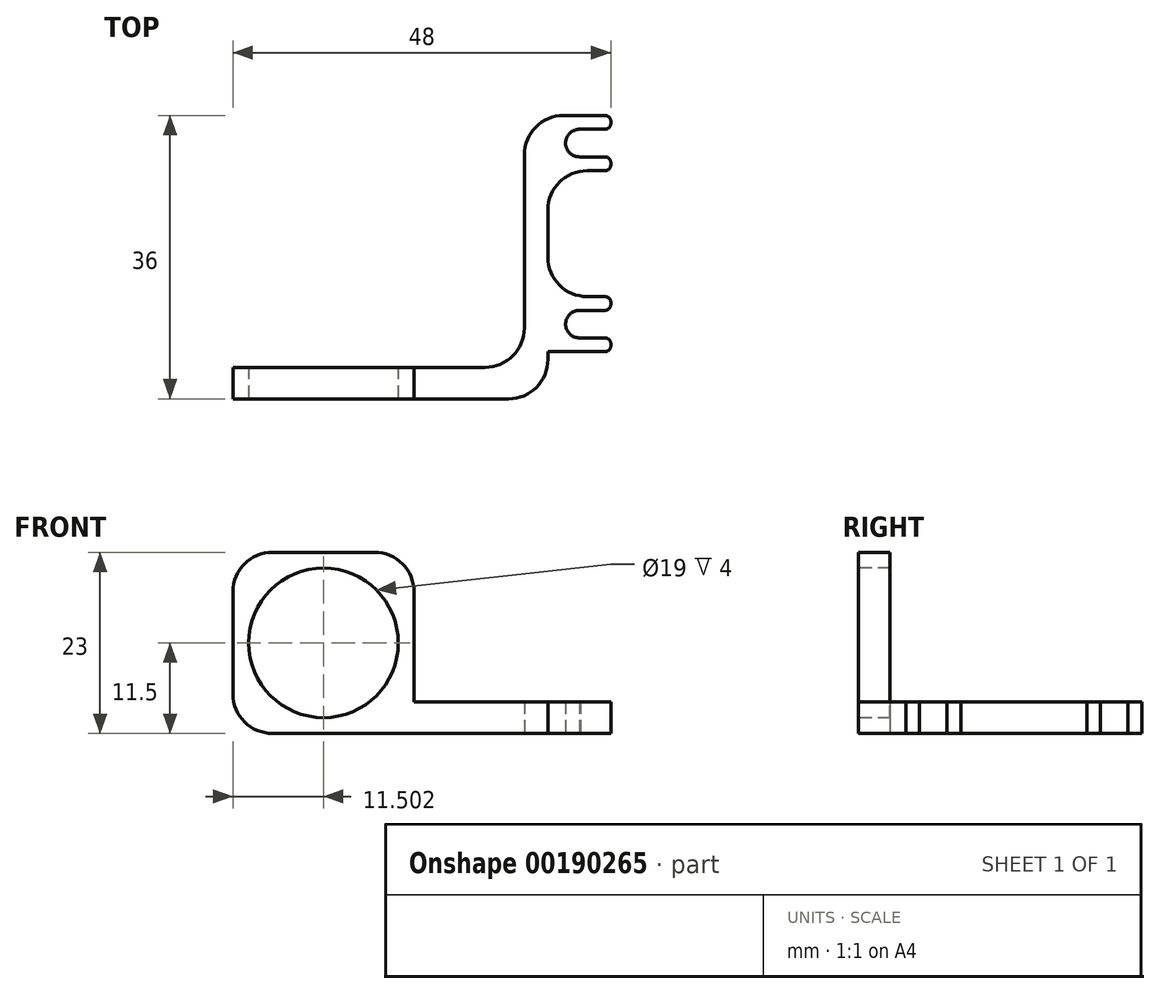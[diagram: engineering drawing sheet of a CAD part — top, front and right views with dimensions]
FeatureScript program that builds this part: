
annotation { "Feature Type Name" : "Feature", "Feature Type Description" : "" }
export const myFeature = defineFeature(function(context is Context, id is Id, definition is map)
    precondition{}
    {
        {
            var Q0;
            Q0=qCreatedBy(makeId("Top.planeOp"),FACE);
            var sketch = newSketch(context, id + "F0", { "sketchPlane" : qUnion([Q0])});
            skLineSegment(sketch, "E0.bottom", {"start": v(-11.59, 10.69) * mm, "end": v(-8.59, 10.69) * mm});
            skLineSegment(sketch, "E0.top", {"start": v(-11.59, -21.31) * mm, "end": v(-8.59, -21.31) * mm});
            skLineSegment(sketch, "E0.left", {"start": v(-11.59, 10.69) * mm, "end": v(-11.59, -21.31) * mm});
            skLineSegment(sketch, "E0.right", {"start": v(-8.59, 10.69) * mm, "end": v(-8.59, -21.31) * mm});
            skLineSegment(sketch, "E1.bottom", {"start": v(-8.59, 10.69) * mm, "end": v(-0.59, 10.69) * mm});
            skLineSegment(sketch, "E1.top", {"start": v(-8.59, 3.69) * mm, "end": v(-0.59, 3.69) * mm});
            skLineSegment(sketch, "E1.left", {"start": v(-8.59, 10.69) * mm, "end": v(-8.59, 3.69) * mm});
            skLineSegment(sketch, "E1.right", {"start": v(-0.59, 10.69) * mm, "end": v(-0.59, 3.69) * mm});
            skLineSegment(sketch, "E2.bottom", {"start": v(-8.59, -12.31) * mm, "end": v(-0.59, -12.31) * mm});
            skLineSegment(sketch, "E2.top", {"start": v(-8.59, -19.31) * mm, "end": v(-0.59, -19.31) * mm});
            skLineSegment(sketch, "E2.left", {"start": v(-8.59, -12.31) * mm, "end": v(-8.59, -19.31) * mm});
            skLineSegment(sketch, "E2.right", {"start": v(-0.59, -12.31) * mm, "end": v(-0.59, -19.31) * mm});
            skLineSegment(sketch, "E3.bottom", {"start": v(-8.59, -21.31) * mm, "end": v(-48.59, -21.31) * mm});
            skLineSegment(sketch, "E3.top", {"start": v(-8.59, -25.31) * mm, "end": v(-48.59, -25.31) * mm});
            skLineSegment(sketch, "E3.left", {"start": v(-8.59, -21.31) * mm, "end": v(-8.59, -25.31) * mm});
            skLineSegment(sketch, "E3.right", {"start": v(-48.59, -21.31) * mm, "end": v(-48.59, -25.31) * mm});
            skLineSegment(sketch, "E4", {"start": v(-8.59, 7.19) * mm, "end": v(11.26, 7.19) * mm, "construction": true});
            skPoint(sketch, "E4.endSnap0", {"position": v(-0.59, 7.19) * mm});
            skLineSegment(sketch, "E5", {"start": v(-8.59, -15.81) * mm, "end": v(12.47, -15.81) * mm, "construction": true});
            skCircle(sketch, "E6", {"center": v(-4.59, 7.19) * mm, "radius": 1.75 * mm});
            skPoint(sketch, "E6.centerSnap0", {"position": v(-4.59, 10.69) * mm});
            skCircle(sketch, "E7", {"center": v(-4.59, -15.81) * mm, "radius": 1.75 * mm});
            skPoint(sketch, "E7.centerSnap0", {"position": v(-4.59, -19.31) * mm});
            skLineSegment(sketch, "E8", {"start": v(-4.63, 5.44) * mm, "end": v(-0.59, 5.44) * mm});
            skLineSegment(sketch, "E9", {"start": v(-4.59, 8.94) * mm, "end": v(-0.59, 8.94) * mm});
            skLineSegment(sketch, "E10", {"start": v(-4.59, -14.06) * mm, "end": v(-0.59, -14.06) * mm});
            skPoint(sketch, "E10.startSnap0", {"position": v(-4.59, -12.31) * mm});
            skLineSegment(sketch, "E11", {"start": v(-4.71, -17.56) * mm, "end": v(-0.59, -17.56) * mm});
            skLineSegment(sketch, "E12", {"start": v(-25.59, -21.31) * mm, "end": v(-25.59, -25.31) * mm});
            skLineSegment(sketch, "E13.bottom", {"start": v(-44.59, -22.81) * mm, "end": v(-29.59, -22.81) * mm});
            skLineSegment(sketch, "E13.top", {"start": v(-44.59, -23.81) * mm, "end": v(-29.59, -23.81) * mm});
            skLineSegment(sketch, "E13.left", {"start": v(-44.59, -22.81) * mm, "end": v(-44.59, -23.81) * mm});
            skLineSegment(sketch, "E13.right", {"start": v(-29.59, -22.81) * mm, "end": v(-29.59, -23.81) * mm});
            skSolve(sketch);
        }
        {
            var Q0;
            Q0=makeQuery(id+"F0.imprint","IMPRINT",FACE,{"disambiguationData":[TD([[makeQuery(id+"F0.imprint","IMPRINT",EDGE,{"derivedFrom":sQuery(id+"F0.wireOp",EDGE,"E0.bottom")}),-1.0]])]});
            var Q1;
            {var subQ1=sQuery(id+"F0.wireOp",EDGE,"E2.bottom");Q1=makeQuery(id+"F0.imprint","IMPRINT",FACE,{"disambiguationData":[TD([[makeQuery(id+"F0.imprint","IMPRINT",EDGE,{"derivedFrom":subQ1}),-1.0]])]});}
            var Q2;
            {var subQ1=sQuery(id+"F0.wireOp",EDGE,"E1.bottom");Q2=makeQuery(id+"F0.imprint","IMPRINT",FACE,{"disambiguationData":[TD([[makeQuery(id+"F0.imprint","IMPRINT",EDGE,{"derivedFrom":subQ1}),-1.0]])]});}
            var Q3;
            {var subQ0=sQuery(id+"F0.wireOp",EDGE,"E3.left");Q3=makeQuery(id+"F0.imprint","IMPRINT",FACE,{"disambiguationData":[TD([[makeQuery(id+"F0.imprint","IMPRINT",EDGE,{"derivedFrom":subQ0}),-1.0]])]});}
            extrude(context, id + "F1", {"entities" : qUnion([Q0, Q1, Q2, Q3]), "depth" : 4 * mm});
        }
        {
            var Q0;
            {var subQ1=sQuery(id+"F0.wireOp",EDGE,"E3.right");Q0=makeQuery(id+"F0.imprint","IMPRINT",FACE,{"disambiguationData":[TD([[makeQuery(id+"F0.imprint","IMPRINT",EDGE,{"derivedFrom":subQ1}),1.0]])]});}
            var Q1;
            Q1=makeQuery(id+"F0.imprint","IMPRINT",FACE,{"disambiguationData":[TD([[makeQuery(id+"F0.imprint","IMPRINT",EDGE,{"derivedFrom":sQuery(id+"F0.wireOp",EDGE,"E13.bottom")}),-1.0]])]});
            extrude(context, id + "F2", {"entities" : qUnion([Q0, Q1]), "operationType" : NewBodyOperationType.ADD, "depth" : 23 * mm});
        }
        {
            var Q0;
            {var subQ0=sQuery(id+"F0.wireOp",EDGE,"E3.top");Q0=makeQuery(id+"F2.boolean.opBoolean","MERGE",FACE,{"derivedFrom":[makeQuery(id+"F1.opExtrude","SWEPT_FACE",FACE,{"disambiguationData":[OSD([subQ0])]}),makeQuery(id+"F2.opExtrude","SWEPT_FACE",FACE,{"disambiguationData":[OSD([subQ0])]})]});}
            var sketch = newSketch(context, id + "F3", { "sketchPlane" : qUnion([Q0])});
            skCircle(sketch, "E14", {"center": v(-37.09, 11.5) * mm, "radius": 9.5 * mm});
            skPoint(sketch, "E14.centerSnap0", {"position": v(-37.09, 23) * mm});
            skPoint(sketch, "E14.centerSnap1", {"position": v(-48.59, 11.5) * mm});
            skSolve(sketch);
        }
        {
            var Q0;
            Q0=makeQuery(id+"F3.imprint","IMPRINT",FACE,{"disambiguationData":[TD([[makeQuery(id+"F3.imprint","IMPRINT",EDGE,{"derivedFrom":sQuery(id+"F3.wireOp",EDGE,"E14")}),1.0]])]});
            extrude(context, id + "F4", {"entities" : qUnion([Q0]), "operationType" : NewBodyOperationType.REMOVE, "oppositeDirection" : true, "depth" : 25 * mm});
        }
        {
            var Q0;
            Q0=makeQuery(id+"F2.opExtrude","CAP_EDGE",EDGE,{"disambiguationData":[OSD([sQuery(id+"F0.wireOp",EDGE,"E3.right")])],"isStart":false});
            var Q1;
            Q1=makeQuery(id+"F2.opExtrude","CAP_EDGE",EDGE,{"disambiguationData":[OSD([sQuery(id+"F0.wireOp",EDGE,"E12")])],"isStart":false});
            var Q2;
            Q2=makeQuery(id+"F2.opExtrude","CAP_EDGE",EDGE,{"disambiguationData":[OSD([sQuery(id+"F0.wireOp",EDGE,"E3.right")])],"isStart":true});
            var Q3;
            Q3=makeQuery(id+"F1.opExtrude","CAP_EDGE",EDGE,{"disambiguationData":[OSD([sQuery(id+"F0.wireOp",EDGE,"E12")])],"isStart":false});
            fillet(context, id + "F5", {"entities" : qUnion([Q0, Q1, Q2, Q3]), "radius" : 5 * mm, "tangentPropagation" : true, "allowEdgeOverflow" : false});
        }
        {
            var Q0;
            Q0=makeQuery(id+"F1.opExtrude","SWEPT_EDGE",EDGE,{"disambiguationData":[OSD([sQuery(id+"F0.wireOp",EDGE,"E3.top"),sQuery(id+"F0.wireOp",EDGE,"E3.left")])]});
            var Q1;
            Q1=makeQuery(id+"F1.opExtrude","SWEPT_EDGE",EDGE,{"disambiguationData":[OSD([sQuery(id+"F0.wireOp",EDGE,"E0.left"),sQuery(id+"F0.wireOp",EDGE,"E3.bottom")])]});
            var Q2;
            Q2=makeQuery(id+"F1.opExtrude","SWEPT_EDGE",EDGE,{"disambiguationData":[OSD([sQuery(id+"F0.wireOp",EDGE,"E0.right"),sQuery(id+"F0.wireOp",EDGE,"E2.bottom"),sQuery(id+"F0.wireOp",EDGE,"E2.left")])]});
            var Q3;
            Q3=makeQuery(id+"F1.opExtrude","SWEPT_EDGE",EDGE,{"disambiguationData":[OSD([sQuery(id+"F0.wireOp",EDGE,"E0.right"),sQuery(id+"F0.wireOp",EDGE,"E1.top"),sQuery(id+"F0.wireOp",EDGE,"E1.left")])]});
            var Q4;
            Q4=makeQuery(id+"F1.opExtrude","SWEPT_EDGE",EDGE,{"disambiguationData":[OSD([sQuery(id+"F0.wireOp",EDGE,"E0.bottom"),sQuery(id+"F0.wireOp",EDGE,"E0.left")])]});
            fillet(context, id + "F6", {"entities" : qUnion([Q0, Q1, Q2, Q3, Q4]), "radius" : 5 * mm, "tangentPropagation" : true, "allowEdgeOverflow" : false});
        }
        {
            var Q0;
            Q0=makeQuery(id+"F1.opExtrude","SWEPT_EDGE",EDGE,{"disambiguationData":[OSD([sQuery(id+"F0.wireOp",EDGE,"E1.bottom"),sQuery(id+"F0.wireOp",EDGE,"E1.right")])]});
            var Q1;
            Q1=makeQuery(id+"F1.opExtrude","SWEPT_EDGE",EDGE,{"disambiguationData":[OSD([sQuery(id+"F0.wireOp",EDGE,"E1.right"),sQuery(id+"F0.wireOp",EDGE,"E9")])]});
            var Q2;
            Q2=makeQuery(id+"F1.opExtrude","SWEPT_EDGE",EDGE,{"disambiguationData":[OSD([sQuery(id+"F0.wireOp",EDGE,"E1.right"),sQuery(id+"F0.wireOp",EDGE,"E8")])]});
            var Q3;
            Q3=makeQuery(id+"F1.opExtrude","SWEPT_EDGE",EDGE,{"disambiguationData":[OSD([sQuery(id+"F0.wireOp",EDGE,"E1.top"),sQuery(id+"F0.wireOp",EDGE,"E1.right")])]});
            var Q4;
            Q4=makeQuery(id+"F1.opExtrude","SWEPT_EDGE",EDGE,{"disambiguationData":[OSD([sQuery(id+"F0.wireOp",EDGE,"E2.bottom"),sQuery(id+"F0.wireOp",EDGE,"E2.right")])]});
            var Q5;
            Q5=makeQuery(id+"F1.opExtrude","SWEPT_EDGE",EDGE,{"disambiguationData":[OSD([sQuery(id+"F0.wireOp",EDGE,"E2.right"),sQuery(id+"F0.wireOp",EDGE,"E10")])]});
            var Q6;
            Q6=makeQuery(id+"F1.opExtrude","SWEPT_EDGE",EDGE,{"disambiguationData":[OSD([sQuery(id+"F0.wireOp",EDGE,"E2.right"),sQuery(id+"F0.wireOp",EDGE,"E11")])]});
            var Q7;
            Q7=makeQuery(id+"F1.opExtrude","SWEPT_EDGE",EDGE,{"disambiguationData":[OSD([sQuery(id+"F0.wireOp",EDGE,"E2.top"),sQuery(id+"F0.wireOp",EDGE,"E2.right")])]});
            fillet(context, id + "F7", {"entities" : qUnion([Q0, Q1, Q2, Q3, Q4, Q5, Q6, Q7]), "radius" : .75 * mm, "tangentPropagation" : true, "allowEdgeOverflow" : false});
        }
    });
